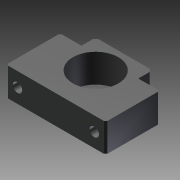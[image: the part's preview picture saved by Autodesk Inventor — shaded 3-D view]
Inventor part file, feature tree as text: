
AUTODESK INVENTOR PART (.ipt)
format: ipt  version: 2011 SP1 (Build 150282100, 282)  size: 113,664 bytes
history: native  units: mm
features: other x14, sketch x4, hole x3, extrude x1
ambient origin geometry x8: Origin, YZ Plane, XZ Plane, XY Plane, X Axis, Y Axis, Z Axis, Center Point
bodies: Solid1 (feature_tree)
feature tree (22):
  extrude  "Extrusion1"  TaperAngle=0.0deg  [1 undecoded]
  hole  "Hole1"  [1 undecoded]
  hole  "Hole2"  [1 undecoded]
  hole  "Hole3"  [1 undecoded]
  other  "bf_1_XY"
  other  "bf_1_YZ"
  other  "bf_1_ZX"
  other  "bf_1_X"
  other  "bf_1_Y"
  other  "bf_1_Z"
  other  "bf_1_Center"
  other  "bf_2x_XY"
  other  "bf_2x_YZ"
  other  "bf_2x_ZX"
  other  "bf_2x_X"
  other  "bf_2x_Y"
  other  "bf_2x_Z"
  other  "bf_2x_Center"
  sketch  "Sketch_1"  dims[d0=20.0mm d1=0.0mm]
  sketch  "Sketch2"  dims[d2=6.6mm d3=6.0mm d4=11.0mm d5=6.5mm d6=90.0deg d7=38.0mm d8=0.0mm]
  sketch  "Sketch3"  dims[d9=6.6mm d10=6.0mm d11=11.0mm d12=6.5mm d13=90.0deg d14=38.0mm d15=0.0mm]
  sketch  "Sketch4"  dims[d16=32.0mm d17=6.0mm d18=4.0mm d19=2.0mm d20=90.0deg d21=20.0mm d22=0.0mm d23=0.0mm]
note: 4 required parameter values undecoded (feature->parameter linkage not recoverable at this tier; creation-order binding heuristic only, values carry confidence <= 0.55)
